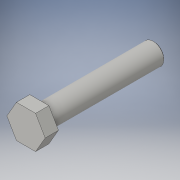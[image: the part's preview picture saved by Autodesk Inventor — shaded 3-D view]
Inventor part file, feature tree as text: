
AUTODESK INVENTOR PART (.ipt)
format: ipt  version: 2016 (Build 200138000, 138)  size: 102,912 bytes
history: native  units: in
note: dims shown in document units (in); Inventor stores cm internally (conversion verified against a paired STEP export)
features: extrude x2, sketch x2, chamfer x1
ambient origin geometry x8: Origin, YZ Plane, XZ Plane, XY Plane, X Axis, Y Axis, Z Axis, Center Point
bodies: Solid1 (feature_tree)
feature tree (5):
  extrude  "Extrusion1"  Depth=1.5in TaperAngle=0.0deg
  extrude  "Extrusion2"  Depth=0.125in TaperAngle=45.0deg
  chamfer  "Chamfer1"  [1 undecoded]
  sketch  "Sketch1"  dims[d0=0.25in d1=1.5in d2=0.0in]
  sketch  "Sketch2"  dims[d3=0.1562in d4=0.0in d5=0.01in d6=0.125in d7=45.0deg]
note: 1 required parameter value undecoded (feature->parameter linkage not recoverable at this tier; creation-order binding heuristic only, values carry confidence <= 0.55)
